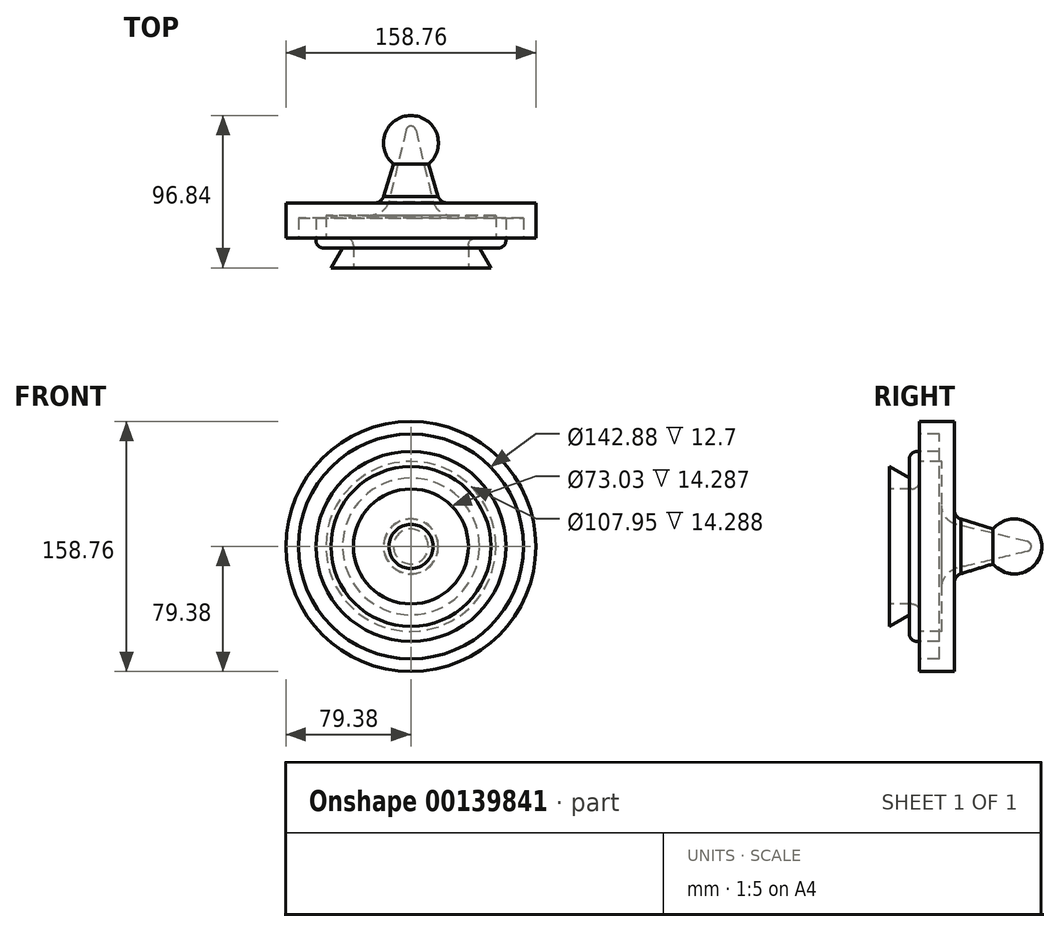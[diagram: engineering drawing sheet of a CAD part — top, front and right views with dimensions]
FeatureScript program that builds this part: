
annotation { "Feature Type Name" : "Feature", "Feature Type Description" : "" }
export const myFeature = defineFeature(function(context is Context, id is Id, definition is map)
    precondition{}
    {
        {
            var Q0;
            Q0=qCreatedBy(makeId("Right.planeOp"),FACE);
            var sketch = newSketch(context, id + "F0", { "sketchPlane" : qUnion([Q0])});
            skLineSegment(sketch, "E0", {"start": v(0, 79.38) * mm, "end": v(-22.23, 79.38) * mm});
            skLineSegment(sketch, "E1", {"start": v(-22.23, 79.38) * mm, "end": v(-22.23, 71.44) * mm});
            skLineSegment(sketch, "E2", {"start": v(-22.23, 71.44) * mm, "end": v(-9.53, 71.44) * mm});
            skLineSegment(sketch, "E3", {"start": v(-9.53, 71.44) * mm, "end": v(-9.52, 60.33) * mm});
            skLineSegment(sketch, "E4", {"start": v(-9.52, 60.33) * mm, "end": v(-23.81, 60.32) * mm});
            skLineSegment(sketch, "E5", {"start": v(-28.58, 55.56) * mm, "end": v(-28.58, 43.47) * mm});
            skLineSegment(sketch, "E6", {"start": v(-28.57, 43.47) * mm, "end": v(-41.28, 50.8) * mm});
            skLineSegment(sketch, "E7", {"start": v(-41.28, 50.8) * mm, "end": v(-41.28, 36.51) * mm});
            skLineSegment(sketch, "E8", {"start": v(-41.27, 36.51) * mm, "end": v(-26.99, 36.51) * mm});
            skLineSegment(sketch, "E9", {"start": v(-22.22, 41.27) * mm, "end": v(-22.23, 53.97) * mm});
            skLineSegment(sketch, "E10", {"start": v(-22.23, 53.97) * mm, "end": v(-7.94, 53.97) * mm});
            skLineSegment(sketch, "E11", {"start": v(-7.94, 53.97) * mm, "end": v(-7.94, 26.07) * mm});
            skLineSegment(sketch, "E12", {"start": v(0.72, 14.03) * mm, "end": v(46.41, 3.09) * mm});
            skLineSegment(sketch, "E13", {"start": v(0, 23.25) * mm, "end": v(0, 79.38) * mm});
            skPoint(sketch, "E14.start.orphan", {"position": v(0, 14.29) * mm});
            skArc(sketch, "E15", {"start": v(55.56, 0) * mm, "mid": v(43.99, 16.44) * mm, "end": v(24.6, 11.08) * mm});
            skPoint(sketch, "E16.visualSharp", {"position": v(-7.94, 16.94) * mm});
            skArc(sketch, "E16.filletArc", {"start": v(-7.94, 26.07) * mm, "mid": v(-5.55, 18.66) * mm, "end": v(0.72, 14.03) * mm});
            skPoint(sketch, "E17.visualSharp", {"position": v(0, 18.7) * mm});
            skArc(sketch, "E17.filletArc", {"start": v(0, 23.25) * mm, "mid": v(1.13, 19.63) * mm, "end": v(4.13, 17.3) * mm});
            skPoint(sketch, "E18.end.orphan", {"position": v(16.88, 0) * mm});
            skPoint(sketch, "E19.visualSharp", {"position": v(-28.58, 60.32) * mm});
            skArc(sketch, "E19.filletArc", {"start": v(-23.81, 60.32) * mm, "mid": v(-27.18, 58.93) * mm, "end": v(-28.58, 55.56) * mm});
            skPoint(sketch, "E20.visualSharp", {"position": v(-22.22, 36.51) * mm});
            skArc(sketch, "E20.filletArc", {"start": v(-26.99, 36.51) * mm, "mid": v(-23.62, 37.9) * mm, "end": v(-22.22, 41.27) * mm});
            skArc(sketch, "E21.MirrorCS", {"start": v(46.41, 3.09) * mm, "mid": v(48.17, 1.97) * mm, "end": v(48.85, 0) * mm});
            skPoint(sketch, "E22.orphan", {"position": v(24.6, 10.43) * mm});
            skLineSegment(sketch, "E23", {"start": v(4.13, 17.3) * mm, "end": v(24.6, 11.08) * mm});
            skLineSegment(sketch, "E24", {"start": v(48.85, 0) * mm, "end": v(55.56, 0) * mm});
            skSolve(sketch);
        }
        {
            var Q0;
            Q0=makeQuery(id+"F0.imprint","IMPRINT",FACE,{"disambiguationData":[TD([[makeQuery(id+"F0.imprint","IMPRINT",EDGE,{"derivedFrom":sQuery(id+"F0.wireOp",EDGE,"E0")}),1.0]])]});
            var Q1;
            Q1=sQuery(id+"F0.wireOp",EDGE,"E24");
            revolve(context, id + "F1", {"entities" : qUnion([Q0]), "axis" : qUnion([Q1]), "revolveType" : RevolveType.FULL});
        }
    });
